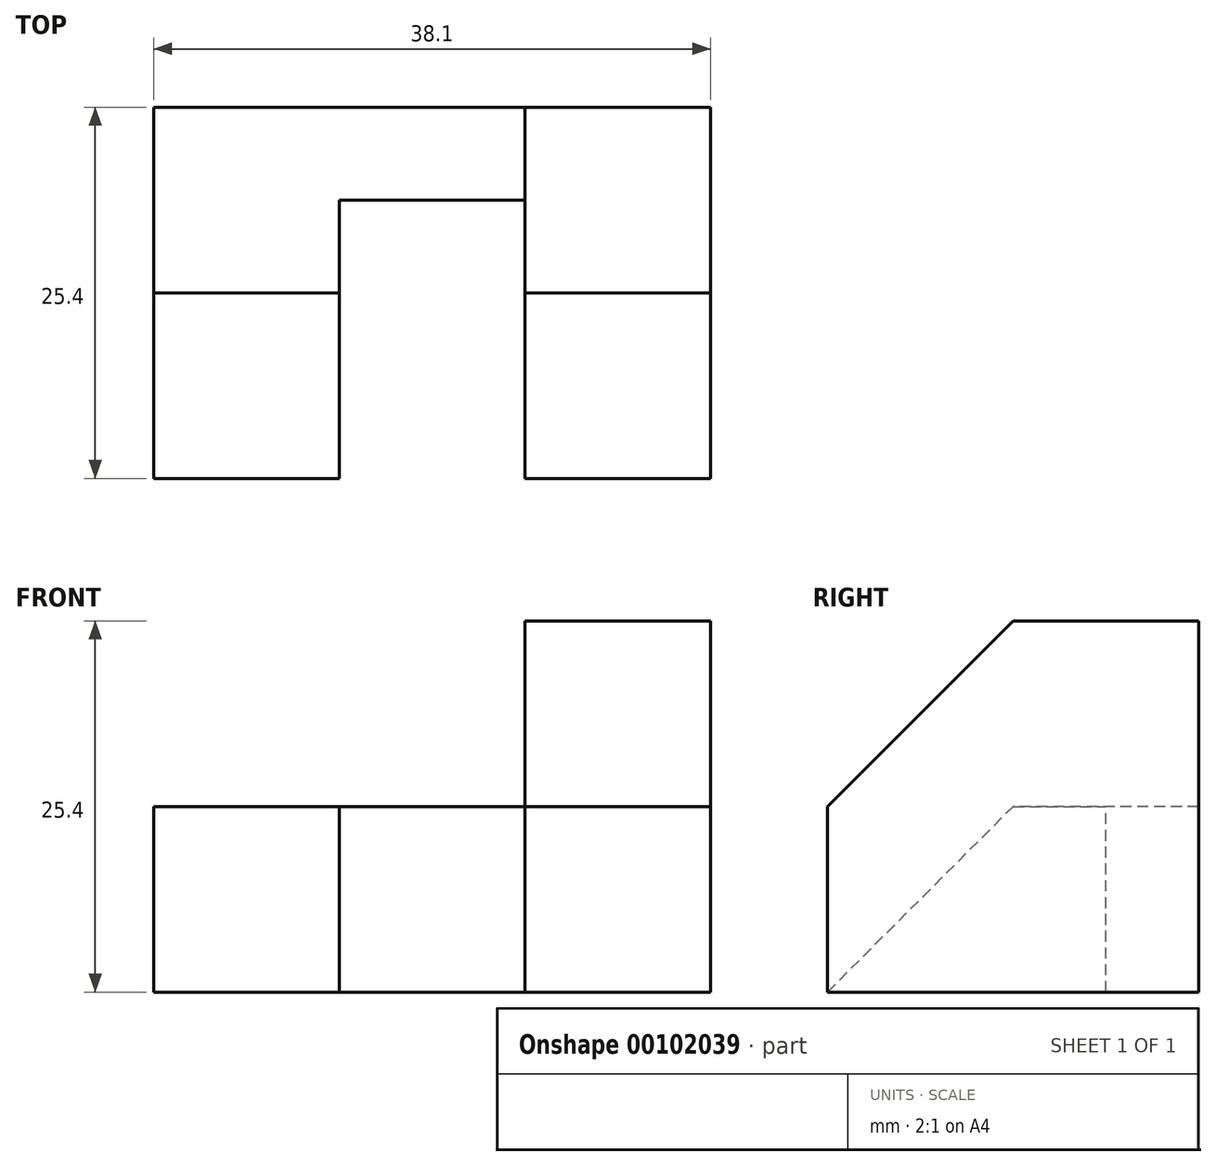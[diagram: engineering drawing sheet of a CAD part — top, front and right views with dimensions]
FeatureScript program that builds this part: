
annotation { "Feature Type Name" : "Feature", "Feature Type Description" : "" }
export const myFeature = defineFeature(function(context is Context, id is Id, definition is map)
    precondition{}
    {
        {
            var Q0;
            Q0=qCreatedBy(makeId("Right.planeOp"),FACE);
            var sketch = newSketch(context, id + "F0", { "sketchPlane" : qUnion([Q0])});
            skLineSegment(sketch, "E0", {"start": v(0, 0) * mm, "end": v(0, 12.7) * mm});
            skLineSegment(sketch, "E1", {"start": v(0, 12.7) * mm, "end": v(12.7, 25.4) * mm});
            skLineSegment(sketch, "E2", {"start": v(12.7, 25.4) * mm, "end": v(25.4, 25.4) * mm});
            skLineSegment(sketch, "E3", {"start": v(25.4, 25.4) * mm, "end": v(25.4, 0) * mm});
            skLineSegment(sketch, "E4", {"start": v(25.4, 0) * mm, "end": v(0, 0) * mm});
            skSolve(sketch);
        }
        {
            var Q0;
            Q0 = qSketchRegion(id + "F0", true);
            var Q1;
            Q1=makeQuery(id+"F0.imprint","IMPRINT",FACE,{"disambiguationData":[TD([[makeQuery(id+"F0.imprint","IMPRINT",EDGE,{"derivedFrom":sQuery(id+"F0.wireOp",EDGE,"E0")}),-1.0]])]});
            extrude(context, id + "F1", {"entities" : qUnion([Q0, Q1]), "depth" : 12.7 * mm});
        }
        {
            var Q0;
            Q0=makeQuery(id+"F1.opExtrude","CAP_FACE",FACE,{"disambiguationData":[OSD([sQuery(id+"F0.wireOp",EDGE,"E0"),sQuery(id+"F0.wireOp",EDGE,"E1"),sQuery(id+"F0.wireOp",EDGE,"E2"),sQuery(id+"F0.wireOp",EDGE,"E3"),sQuery(id+"F0.wireOp",EDGE,"E4")])],"isStart":true});
            var sketch = newSketch(context, id + "F2", { "sketchPlane" : qUnion([Q0])});
            skLineSegment(sketch, "E5.bottom", {"start": v(-25.4, 0) * mm, "end": v(-19.05, 0) * mm});
            skLineSegment(sketch, "E5.top", {"start": v(-25.4, 12.7) * mm, "end": v(-19.05, 12.7) * mm});
            skLineSegment(sketch, "E5.left", {"start": v(-25.4, 0) * mm, "end": v(-25.4, 12.7) * mm});
            skLineSegment(sketch, "E5.right", {"start": v(-19.05, 0) * mm, "end": v(-19.05, 12.7) * mm});
            skSolve(sketch);
        }
        {
            var Q0;
            Q0 = qSketchRegion(id + "F2", true);
            extrude(context, id + "F3", {"entities" : qUnion([Q0]), "operationType" : NewBodyOperationType.ADD, "depth" : 12.7 * mm});
        }
        {
            var Q0;
            Q0=qCreatedBy(makeId("Top.planeOp"),FACE);
            var sketch = newSketch(context, id + "F4", { "sketchPlane" : qUnion([Q0])});
            skLineSegment(sketch, "E6", {"start": v(-12.7, 25.4) * mm, "end": v(-25.4, 25.4) * mm});
            skLineSegment(sketch, "E7", {"start": v(-25.4, 25.4) * mm, "end": v(-25.4, 0) * mm});
            skLineSegment(sketch, "E8", {"start": v(-25.4, 0) * mm, "end": v(-12.7, 0) * mm});
            skLineSegment(sketch, "E9", {"start": v(-12.7, 0) * mm, "end": v(-12.7, 25.4) * mm});
            skSolve(sketch);
        }
        {
            var Q0;
            Q0 = qSketchRegion(id + "F4", true);
            extrude(context, id + "F5", {"entities" : qUnion([Q0]), "operationType" : NewBodyOperationType.ADD, "depth" : 12.7 * mm});
        }
        {
            var Q0;
            Q0=makeQuery(id+"F5.opExtrude","SWEPT_FACE",FACE,{"disambiguationData":[OSD([sQuery(id+"F4.wireOp",EDGE,"E7")])]});
            var sketch = newSketch(context, id + "F6", { "sketchPlane" : qUnion([Q0])});
            skLineSegment(sketch, "E10", {"start": v(-12.7, 12.7) * mm, "end": v(0, 0) * mm});
            skLineSegment(sketch, "E11", {"start": v(0, 0) * mm, "end": v(0, 12.7) * mm});
            skLineSegment(sketch, "E12", {"start": v(0, 12.7) * mm, "end": v(-12.7, 12.7) * mm});
            skSolve(sketch);
        }
        {
            var Q0;
            Q0=makeQuery(id+"F6.imprint","IMPRINT",FACE,{"disambiguationData":[TD([[makeQuery(id+"F6.imprint","IMPRINT",EDGE,{"derivedFrom":sQuery(id+"F6.wireOp",EDGE,"E10")}),1.0]])]});
            extrude(context, id + "F7", {"entities" : qUnion([Q0]), "operationType" : NewBodyOperationType.REMOVE, "endBound" : BoundingType.UP_TO_NEXT, "oppositeDirection" : true, "depth" : 25.4 * mm});
        }
    });
